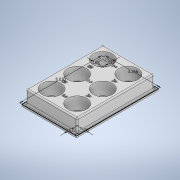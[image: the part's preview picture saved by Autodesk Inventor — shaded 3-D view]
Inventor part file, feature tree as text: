
AUTODESK INVENTOR PART (.ipt)
format: ipt  version: 2020 (Build 240168000, 168)  size: 600,576 bytes
history: native  units: in
note: dims shown in document units (in); Inventor stores cm internally (conversion verified against a paired STEP export)
features: extrude x5, sketch x4, fillet x3
ambient origin geometry x8: Origin, YZ Plane, XZ Plane, XY Plane, X Axis, Y Axis, Z Axis, Center Point
bodies: Solid1 (feature_tree)
feature tree (12):
  sketch  "Sketch1"  dims[d0=3.3661in d1=5.0295in]
  extrude  "Extrusion1"  Depth=5.0295in
  extrude  "Extrusion2"  Depth=0.1526in
  extrude  "Extrusion3"  Depth=0.1526in
  extrude  "Extrusion4"  Depth=0.1181in TaperAngle=0.0deg
  fillet  "Fillet1"  Radius=0.7874in
  fillet  "Fillet2"  Radius=0.7874in
  fillet  "Fillet3"  Radius=1.1811in
  extrude  "Extrusion5"  Depth=0.7874in
  sketch  "Sketch2"  dims[d2=0.1083in d3=0.1526in]
  sketch  "Sketch3"  dims[d4=0.1083in d5=0.1526in]
  sketch  "Sketch4"  dims[d6=0.7874in d7=0.0in d8=0.1181in d9=0.0in d10=0.7874in d11=0.7874in d12=1.1811in d13=0.7874in d15=1.5748in d16=1.1811in d18=1.5748in d21=0.7874in d22=0.0in d23=1.2992in d24=0.7874in d26=1.5748in d27=1.1811in d29=1.5748in d32=0.1181in d33=0.1181in d34=0.1181in d35=0.1181in d36=0.7087in d37=0.0in d38=0.125in d39=0.125in d40=0.0787in d41=0.0394in d42=0.0in]
